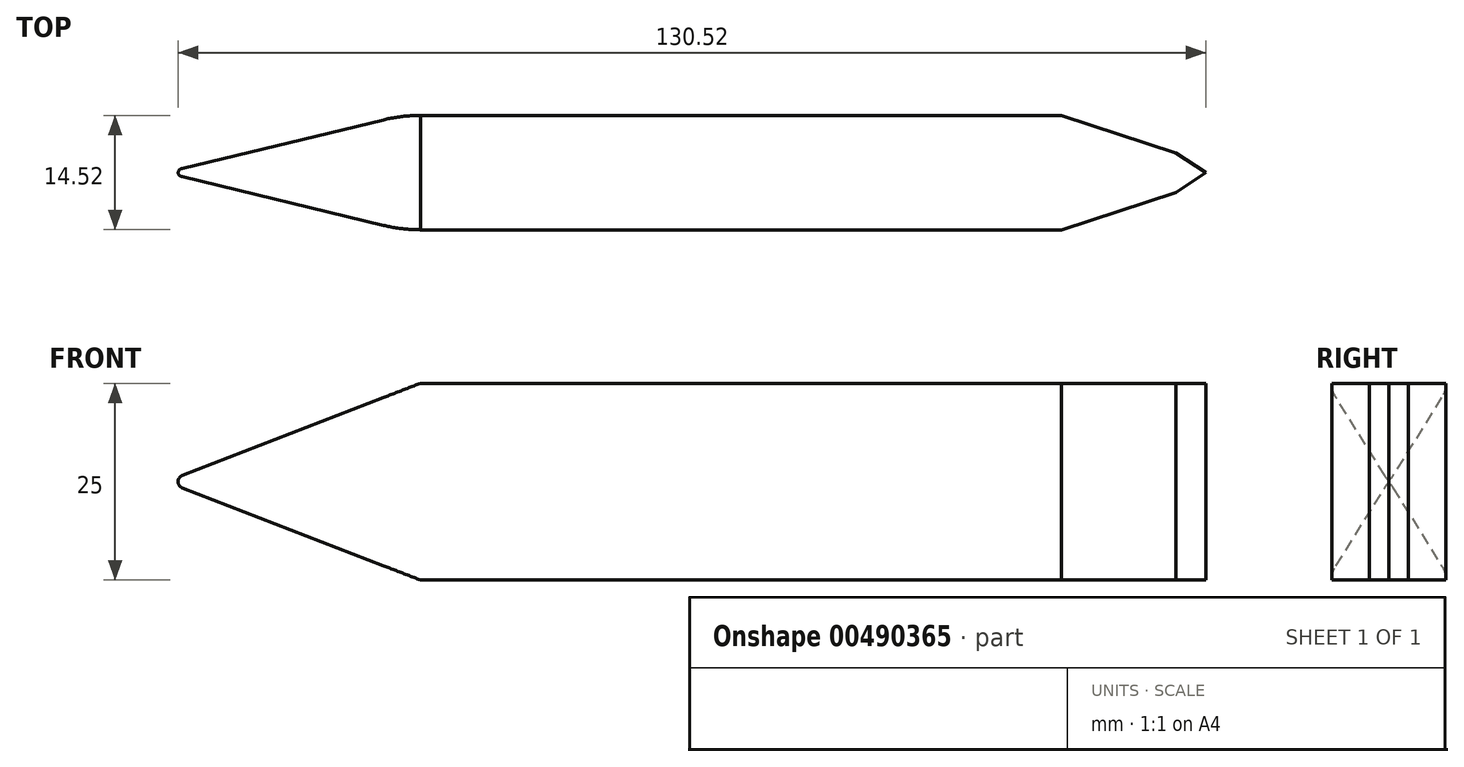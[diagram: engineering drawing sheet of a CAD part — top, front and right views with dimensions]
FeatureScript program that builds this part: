
annotation { "Feature Type Name" : "Feature", "Feature Type Description" : "" }
export const myFeature = defineFeature(function(context is Context, id is Id, definition is map)
    precondition{}
    {
        {
            var Q0;
            Q0=qCreatedBy(makeId("Top.planeOp"),FACE);
            var sketch = newSketch(context, id + "F0", { "sketchPlane" : qUnion([Q0])});
            skLineSegment(sketch, "E0.bottom", {"start": v(41.9, 7.26) * mm, "end": v(-39.52, 7.26) * mm});
            skLineSegment(sketch, "E0.top", {"start": v(41.9, -7.26) * mm, "end": v(-39.52, -7.26) * mm});
            skPoint(sketch, "E0.middle", {"position": v(0, 0) * mm});
            skLineSegment(sketch, "E1", {"start": v(41.9, 7.26) * mm, "end": v(56.43, 2.5) * mm});
            skLineSegment(sketch, "E2", {"start": v(56.43, 2.5) * mm, "end": v(60.24, 0) * mm});
            skLineSegment(sketch, "E3", {"start": v(60.24, 0) * mm, "end": v(56.43, -2.5) * mm});
            skLineSegment(sketch, "E4", {"start": v(41.9, -7.26) * mm, "end": v(56.43, -2.5) * mm});
            skLineSegment(sketch, "E5", {"start": v(-44.22, 6.7) * mm, "end": v(-69.9, 0.49) * mm});
            skLineSegment(sketch, "E6", {"start": v(-69.9, -0.49) * mm, "end": v(-44.22, -6.7) * mm});
            skPoint(sketch, "E7.visualSharp", {"position": v(-71.9, 0) * mm});
            skArc(sketch, "E7.filletArc", {"start": v(-69.9, 0.49) * mm, "mid": v(-70.28, 0) * mm, "end": v(-69.9, -0.49) * mm});
            skPoint(sketch, "E8.visualSharp", {"position": v(-41.9, 7.26) * mm});
            skArc(sketch, "E8.filletArc", {"start": v(-39.52, 7.26) * mm, "mid": v(-41.89, 7.12) * mm, "end": v(-44.22, 6.7) * mm});
            skPoint(sketch, "E9.visualSharp", {"position": v(-41.9, -7.26) * mm});
            skArc(sketch, "E9.filletArc", {"start": v(-44.22, -6.7) * mm, "mid": v(-41.89, -7.12) * mm, "end": v(-39.52, -7.26) * mm});
            skSolve(sketch);
        }
        {
            var Q0;
            Q0 = qSketchRegion(id + "F0", true);
            extrude(context, id + "F1", {"entities" : qUnion([Q0]), "depth" : 25 * mm});
        }
        {
            var Q0;
            Q0=makeQuery(id+"F1.opExtrude","SWEPT_FACE",FACE,{"disambiguationData":[OSD([sQuery(id+"F0.wireOp",EDGE,"E0.top")])]});
            var sketch = newSketch(context, id + "F2", { "sketchPlane" : qUnion([Q0])});
            skLineSegment(sketch, "E10", {"start": v(-39.52, 25) * mm, "end": v(-69.76, 13.3) * mm});
            skLineSegment(sketch, "E11", {"start": v(-69.76, 11.7) * mm, "end": v(-39.52, 0) * mm});
            skPoint(sketch, "E12.visualSharp", {"position": v(-71.8, 12.5) * mm});
            skArc(sketch, "E12.filletArc", {"start": v(-69.76, 13.3) * mm, "mid": v(-70.3, 12.5) * mm, "end": v(-69.76, 11.7) * mm});
            skLineSegment(sketch, "E13", {"start": v(-39.52, 25) * mm, "end": v(-72.55, 25) * mm});
            skLineSegment(sketch, "E14", {"start": v(-72.55, 25) * mm, "end": v(-72.55, 0) * mm});
            skLineSegment(sketch, "E15", {"start": v(-72.55, 0) * mm, "end": v(-39.52, 0) * mm});
            skSolve(sketch);
        }
        {
            var Q0;
            Q0 = qSketchRegion(id + "F2", true);
            extrude(context, id + "F3", {"entities" : qUnion([Q0]), "operationType" : NewBodyOperationType.REMOVE, "endBound" : BoundingType.THROUGH_ALL, "oppositeDirection" : true, "depth" : 25 * mm});
        }
    });
